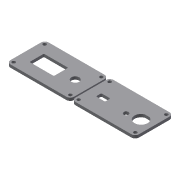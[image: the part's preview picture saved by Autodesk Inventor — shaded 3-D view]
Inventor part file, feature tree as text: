
AUTODESK INVENTOR PART (.ipt)
format: ipt  version: 2015 (Build 190159000, 159)  size: 160,768 bytes
history: native  units: mm
features: extrude x2, sketch x2, projected_geometry x1
ambient origin geometry x8: Origin, YZ Plane, XZ Plane, XY Plane, X Axis, Y Axis, Z Axis, Center Point
bodies: Solid1 (feature_tree)
feature tree (5):
  extrude  "Extrusion1"  Depth=3.0mm
  extrude  "Extrusion2"  [1 undecoded]
  sketch  "Sketch1"  dims[d0=3.0mm d1=0.0mm d2=28.7mm]
  sketch  "Sketch2"  dims[d5=3.0mm d6=0.0mm]
  projected_geometry  "Projected Loop1"
note: 1 required parameter value undecoded (feature->parameter linkage not recoverable at this tier; creation-order binding heuristic only, values carry confidence <= 0.55)
